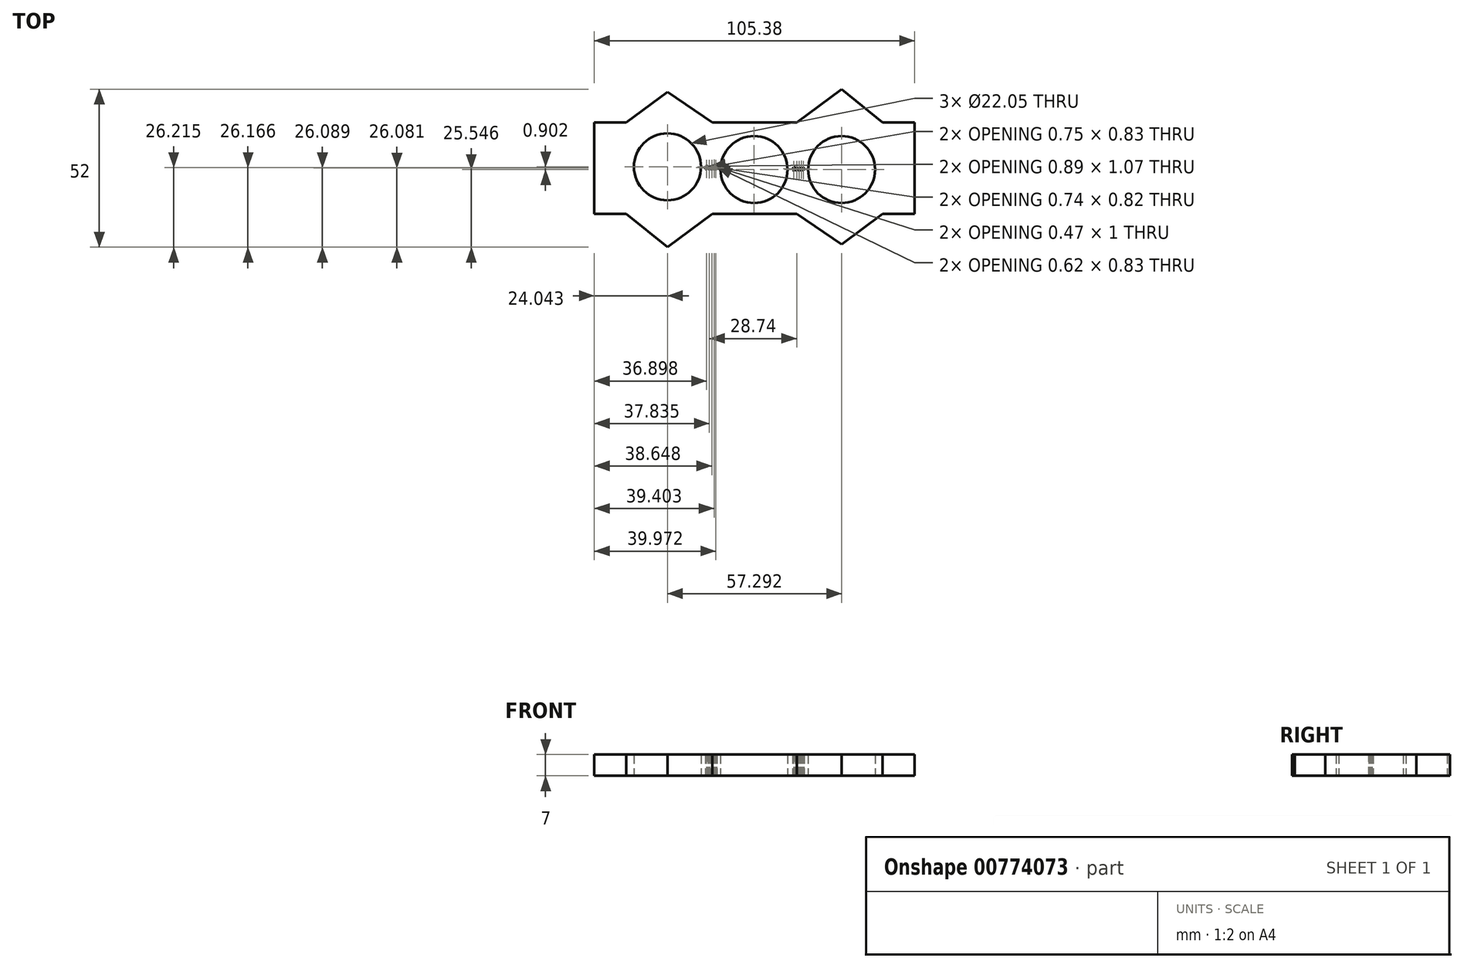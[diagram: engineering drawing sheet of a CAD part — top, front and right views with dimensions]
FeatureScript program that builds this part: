
annotation { "Feature Type Name" : "Feature", "Feature Type Description" : "" }
export const myFeature = defineFeature(function(context is Context, id is Id, definition is map)
    precondition{}
    {
        {
            var Q0;
            Q0=qCreatedBy(makeId("Top.planeOp"),FACE);
            var sketch = newSketch(context, id + "F0", { "sketchPlane" : qUnion([Q0])});
            skLineSegment(sketch, "E0", {"start": v(-75, 23.72) * mm, "end": v(-75, -6.28) * mm});
            skLineSegment(sketch, "E1", {"start": v(-75, 23.72) * mm, "end": v(-64.47, 23.72) * mm});
            skLineSegment(sketch, "E2", {"start": v(-75, -6.28) * mm, "end": v(-64.47, -6.28) * mm});
            skLineSegment(sketch, "E3", {"start": v(-64.47, -6.28) * mm, "end": v(-50.95, -17.28) * mm});
            skLineSegment(sketch, "E4", {"start": v(-50.95, -17.28) * mm, "end": v(-36.22, -6.28) * mm});
            skLineSegment(sketch, "E5", {"start": v(-36.22, -6.28) * mm, "end": v(-21.2, -6.28) * mm});
            skLineSegment(sketch, "E6", {"start": v(-64.47, 23.72) * mm, "end": v(-50.95, 33.82) * mm});
            skLineSegment(sketch, "E7", {"start": v(-50.95, 33.82) * mm, "end": v(-36.22, 23.72) * mm});
            skLineSegment(sketch, "E8", {"start": v(-36.22, 23.72) * mm, "end": v(-21.2, 23.72) * mm});
            skCircle(sketch, "E9", {"center": v(-50.95, 9.17) * mm, "radius": 11.03 * mm});
            skLineSegment(sketch, "E10", {"start": v(30.4, -6.28) * mm, "end": v(30.4, 23.72) * mm});
            skLineSegment(sketch, "E11", {"start": v(30.4, -6.28) * mm, "end": v(19.87, -6.28) * mm});
            skLineSegment(sketch, "E12", {"start": v(30.4, 23.72) * mm, "end": v(19.87, 23.72) * mm});
            skLineSegment(sketch, "E13", {"start": v(19.87, 23.72) * mm, "end": v(6.35, 34.72) * mm});
            skLineSegment(sketch, "E14", {"start": v(6.35, 34.72) * mm, "end": v(-8.38, 23.72) * mm});
            skLineSegment(sketch, "E15", {"start": v(-8.38, 23.72) * mm, "end": v(-23.41, 23.72) * mm});
            skLineSegment(sketch, "E16", {"start": v(19.87, -6.28) * mm, "end": v(6.35, -16.39) * mm});
            skLineSegment(sketch, "E17", {"start": v(6.35, -16.39) * mm, "end": v(-8.38, -6.28) * mm});
            skLineSegment(sketch, "E18", {"start": v(-8.38, -6.28) * mm, "end": v(-23.41, -6.28) * mm});
            skCircle(sketch, "E19", {"center": v(6.35, 8.27) * mm, "radius": 11.03 * mm});
            skCircle(sketch, "E20", {"center": v(-22.45, 8.27) * mm, "radius": 11.03 * mm});
            skText(sketch, "E21", { "text": "Dante\n", "fontName": "OpenSans-Italic.ttf"});
            skText(sketch, "E22", { "text": "Dante", "fontName": "OpenSans-Italic.ttf"});
            const initialGuessF0  = {"E21": [-0.0386, 0.0084, 1, 0, 0.00108], "E22": [-0.00986, 0.008, 1, 0, 0.00108]};
            skSetInitialGuess(sketch, initialGuessF0);
            skSolve(sketch);
        }
        {
            var Q0;
            Q0 = qSketchRegion(id + "F0", true);
            extrude(context, id + "F1", {"entities" : qUnion([Q0]), "depth" : 7 * mm, "offsetDistance" : 25 * mm});
        }
    });
